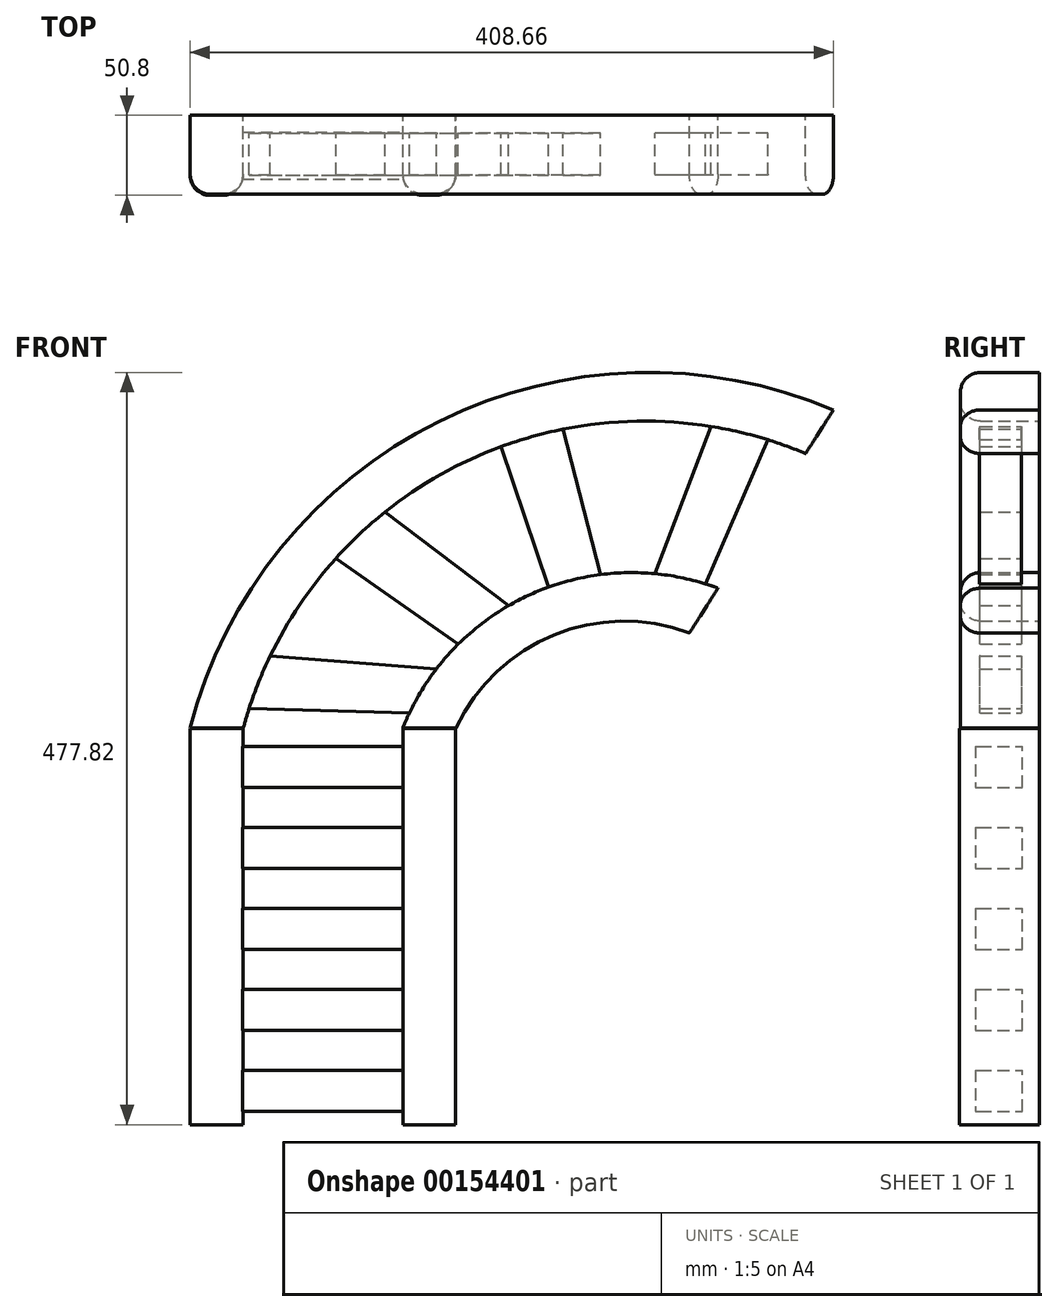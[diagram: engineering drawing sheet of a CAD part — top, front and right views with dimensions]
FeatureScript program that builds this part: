
annotation { "Feature Type Name" : "Feature", "Feature Type Description" : "" }
export const myFeature = defineFeature(function(context is Context, id is Id, definition is map)
    precondition{}
    {
        {
            var Q0;
            Q0=qCreatedBy(makeId("Front.planeOp"),FACE);
            var sketch = newSketch(context, id + "F0", { "sketchPlane" : qUnion([Q0])});
            skLineSegment(sketch, "E0.bottom", {"start": v(-91.03, -95.5) * mm, "end": v(-57.46, -95.5) * mm});
            skLineSegment(sketch, "E0.top", {"start": v(-91.03, 156.28) * mm, "end": v(-57.46, 156.28) * mm});
            skLineSegment(sketch, "E0.left", {"start": v(-91.03, -95.5) * mm, "end": v(-91.03, 156.28) * mm});
            skLineSegment(sketch, "E0.right", {"start": v(-57.46, -95.5) * mm, "end": v(-57.46, 156.28) * mm});
            skLineSegment(sketch, "E1.bottom", {"start": v(44.14, -95.5) * mm, "end": v(77.55, -95.5) * mm});
            skLineSegment(sketch, "E1.top", {"start": v(44.14, 156.28) * mm, "end": v(77.55, 156.28) * mm});
            skLineSegment(sketch, "E1.left", {"start": v(44.14, -95.5) * mm, "end": v(44.14, 156.28) * mm});
            skLineSegment(sketch, "E1.right", {"start": v(77.55, -95.5) * mm, "end": v(77.55, 156.28) * mm});
            skSolve(sketch);
        }
        {
            var Q0;
            Q0=qSketchRegion(id+"F0",true);
            extrude(context, id + "F1", {"entities" : qUnion([Q0]), "depth" : 50.8 * mm});
        }
        {
            var Q0;
            Q0=qCreatedBy(makeId("Front.planeOp"),FACE);
            var sketch = newSketch(context, id + "F2", { "sketchPlane" : qUnion([Q0])});
            skLineSegment(sketch, "E2.bottom", {"start": v(-57.93, -87.01) * mm, "end": v(44.5, -87.01) * mm});
            skLineSegment(sketch, "E2.top", {"start": v(-57.93, -60.98) * mm, "end": v(44.5, -60.98) * mm});
            skLineSegment(sketch, "E2.left", {"start": v(-57.93, -87.01) * mm, "end": v(-57.93, -60.98) * mm});
            skLineSegment(sketch, "E2.right", {"start": v(44.5, -87.01) * mm, "end": v(44.5, -60.98) * mm});
            skLineSegment(sketch, "E3.bottom", {"start": v(-57.93, -35.58) * mm, "end": v(44.5, -35.58) * mm});
            skLineSegment(sketch, "E3.top", {"start": v(-57.93, -9.54) * mm, "end": v(44.5, -9.54) * mm});
            skLineSegment(sketch, "E3.left", {"start": v(-57.93, -35.58) * mm, "end": v(-57.93, -9.54) * mm});
            skLineSegment(sketch, "E3.right", {"start": v(44.5, -35.58) * mm, "end": v(44.5, -9.54) * mm});
            skLineSegment(sketch, "E4.bottom", {"start": v(-57.93, 15.86) * mm, "end": v(44.5, 15.86) * mm});
            skLineSegment(sketch, "E4.top", {"start": v(-57.93, 41.9) * mm, "end": v(44.5, 41.9) * mm});
            skLineSegment(sketch, "E4.left", {"start": v(-57.93, 15.86) * mm, "end": v(-57.93, 41.9) * mm});
            skLineSegment(sketch, "E4.right", {"start": v(44.5, 15.86) * mm, "end": v(44.5, 41.9) * mm});
            skLineSegment(sketch, "E5.bottom", {"start": v(-57.93, 67.3) * mm, "end": v(44.5, 67.3) * mm});
            skLineSegment(sketch, "E5.top", {"start": v(-57.93, 93.33) * mm, "end": v(44.5, 93.33) * mm});
            skLineSegment(sketch, "E5.left", {"start": v(-57.93, 67.3) * mm, "end": v(-57.93, 93.33) * mm});
            skLineSegment(sketch, "E5.right", {"start": v(44.5, 67.3) * mm, "end": v(44.5, 93.33) * mm});
            skLineSegment(sketch, "E6.bottom", {"start": v(-57.93, 118.73) * mm, "end": v(44.5, 118.73) * mm});
            skLineSegment(sketch, "E6.top", {"start": v(-57.93, 144.76) * mm, "end": v(44.5, 144.76) * mm});
            skLineSegment(sketch, "E6.left", {"start": v(-57.93, 118.73) * mm, "end": v(-57.93, 144.76) * mm});
            skLineSegment(sketch, "E6.right", {"start": v(44.5, 118.73) * mm, "end": v(44.5, 144.76) * mm});
            skSolve(sketch);
        }
        {
            var Q0;
            Q0=qSketchRegion(id+"F2",true);
            extrude(context, id + "F3", {"entities" : qUnion([Q0]), "operationType" : NewBodyOperationType.ADD, "depth" : 40.64 * mm, "hasSecondDirection" : true, "secondDirectionOppositeDirection" : false, "secondDirectionDepth" : 10.8 * mm});
        }
        {
            var Q0;
            Q0=makeQuery(id+"F1.opExtrude","SWEPT_BODY",BODY,{"disambiguationData":[OSD([sQuery(id+"F0.wireOp",EDGE,"E0.bottom"),sQuery(id+"F0.wireOp",EDGE,"E0.top"),sQuery(id+"F0.wireOp",EDGE,"E0.left"),sQuery(id+"F0.wireOp",EDGE,"E0.right")])]});
            var Q1;
            Q1=qCreatedBy(makeId("Right.planeOp"),FACE);
            mirror(context, id + "F4", {"entities" : qUnion([Q0]), "mirrorPlane" : qUnion([Q1])});
        }
        {
            var Q0;
            Q0=makeQuery(id+"F1.opExtrude","SWEPT_BODY",BODY,{"disambiguationData":[OSD([sQuery(id+"F0.wireOp",EDGE,"E0.bottom"),sQuery(id+"F0.wireOp",EDGE,"E0.top"),sQuery(id+"F0.wireOp",EDGE,"E0.left"),sQuery(id+"F0.wireOp",EDGE,"E0.right")])]});
            var Q1;
            Q1=qCreatedBy(makeId("Top.planeOp"),FACE);
            mirror(context, id + "F5", {"entities" : qUnion([Q0]), "mirrorPlane" : qUnion([Q1])});
        }
        {
            var Q0;
            Q0=makeQuery(id+"F1.opExtrude","SWEPT_BODY",BODY,{"disambiguationData":[OSD([sQuery(id+"F0.wireOp",EDGE,"E0.bottom"),sQuery(id+"F0.wireOp",EDGE,"E0.top"),sQuery(id+"F0.wireOp",EDGE,"E0.left"),sQuery(id+"F0.wireOp",EDGE,"E0.right")])]});
            var Q1;
            Q1=qCreatedBy(makeId("Right.planeOp"),FACE);
            mirror(context, id + "F6", {"entities" : qUnion([Q0]), "mirrorPlane" : qUnion([Q1])});
        }
        {
            var Q0;
            Q0=makeQuery(id+"F6.opPattern","COPY",BODY,{"derivedFrom":makeQuery(id+"F1.opExtrude","SWEPT_BODY",BODY,{"disambiguationData":[OSD([sQuery(id+"F0.wireOp",EDGE,"E0.bottom"),sQuery(id+"F0.wireOp",EDGE,"E0.top"),sQuery(id+"F0.wireOp",EDGE,"E0.left"),sQuery(id+"F0.wireOp",EDGE,"E0.right")])]}),"instanceName":"1"});
            deleteBodies(context, id + "F7", {"entities" : qUnion([Q0])});
        }
        {
            var Q0;
            Q0=makeQuery(id+"F5.opPattern","COPY",BODY,{"derivedFrom":makeQuery(id+"F1.opExtrude","SWEPT_BODY",BODY,{"disambiguationData":[OSD([sQuery(id+"F0.wireOp",EDGE,"E0.bottom"),sQuery(id+"F0.wireOp",EDGE,"E0.top"),sQuery(id+"F0.wireOp",EDGE,"E0.left"),sQuery(id+"F0.wireOp",EDGE,"E0.right")])]}),"instanceName":"1"});
            deleteBodies(context, id + "F8", {"entities" : qUnion([Q0])});
        }
        {
            var Q0;
            Q0=makeQuery(id+"F4.opPattern","COPY",BODY,{"derivedFrom":makeQuery(id+"F1.opExtrude","SWEPT_BODY",BODY,{"disambiguationData":[OSD([sQuery(id+"F0.wireOp",EDGE,"E0.bottom"),sQuery(id+"F0.wireOp",EDGE,"E0.top"),sQuery(id+"F0.wireOp",EDGE,"E0.left"),sQuery(id+"F0.wireOp",EDGE,"E0.right")])]}),"instanceName":"1"});
            deleteBodies(context, id + "F9", {"entities" : qUnion([Q0])});
        }
        {
            var Q0;
            Q0=qCreatedBy(makeId("Front.planeOp"),FACE);
            var sketch = newSketch(context, id + "F10", { "sketchPlane" : qUnion([Q0])});
            skLineSegment(sketch, "E7", {"start": v(-90.93, 156.43) * mm, "end": v(-57.18, 156.43) * mm});
            skArc(sketch, "E8", {"start": v(317.63, 358.53) * mm, "mid": v(67.02, 351.13) * mm, "end": v(-90.93, 156.43) * mm});
            skArc(sketch, "E9", {"start": v(299.95, 330.76) * mm, "mid": v(81.84, 324.62) * mm, "end": v(-57.18, 156.43) * mm});
            skLineSegment(sketch, "E10", {"start": v(317.63, 358.53) * mm, "end": v(299.95, 330.76) * mm});
            skLineSegment(sketch, "E11", {"start": v(44.1, 156.43) * mm, "end": v(77.86, 156.43) * mm});
            skArc(sketch, "E12", {"start": v(244.3, 245.29) * mm, "mid": v(126.08, 241.68) * mm, "end": v(44.1, 156.43) * mm});
            skLineSegment(sketch, "E13", {"start": v(244.3, 245.29) * mm, "end": v(226.17, 216.79) * mm});
            skArc(sketch, "E14", {"start": v(226.17, 216.79) * mm, "mid": v(140.2, 215.61) * mm, "end": v(77.86, 156.43) * mm});
            skSolve(sketch);
        }
        {
            var Q0;
            Q0=qSketchRegion(id+"F10",true);
            extrude(context, id + "F11", {"entities" : qUnion([Q0]), "depth" : 50.16 * mm});
        }
        {
            var Q0;
            Q0=qCreatedBy(makeId("Front.planeOp"),FACE);
            var sketch = newSketch(context, id + "F12", { "sketchPlane" : qUnion([Q0])});
            skLineSegment(sketch, "E15", {"start": v(-58.79, 169.05) * mm, "end": v(51.94, 165.92) * mm});
            skArc(sketch, "E16", {"start": v(-43.86, 202.37) * mm, "mid": v(-52.52, 186.25) * mm, "end": v(-58.79, 169.05) * mm});
            skLineSegment(sketch, "E17", {"start": v(-43.86, 202.37) * mm, "end": v(69.98, 193.7) * mm});
            skArc(sketch, "E18", {"start": v(51.94, 165.92) * mm, "mid": v(61.37, 179.54) * mm, "end": v(69.98, 193.7) * mm});
            skLineSegment(sketch, "E19", {"start": v(-3.25, 267.62) * mm, "end": v(82.83, 207.23) * mm});
            skArc(sketch, "E20", {"start": v(31.11, 295.04) * mm, "mid": v(11.47, 284.41) * mm, "end": v(-3.25, 267.62) * mm});
            skLineSegment(sketch, "E21", {"start": v(31.11, 295.04) * mm, "end": v(115.1, 231.18) * mm});
            skArc(sketch, "E22", {"start": v(82.83, 207.23) * mm, "mid": v(100.38, 217.3) * mm, "end": v(115.1, 231.18) * mm});
            skLineSegment(sketch, "E23", {"start": v(104.23, 342.23) * mm, "end": v(137.7, 242.57) * mm});
            skArc(sketch, "E24", {"start": v(143.94, 353.26) * mm, "mid": v(123.43, 350.1) * mm, "end": v(104.23, 342.23) * mm});
            skLineSegment(sketch, "E25", {"start": v(143.94, 353.26) * mm, "end": v(170.79, 249.56) * mm});
            skArc(sketch, "E26", {"start": v(137.7, 242.57) * mm, "mid": v(154.64, 244.17) * mm, "end": v(170.79, 249.56) * mm});
            skArc(sketch, "E27", {"start": v(279.48, 347.83) * mm, "mid": v(262.24, 354.81) * mm, "end": v(244.09, 358.84) * mm});
            skLineSegment(sketch, "E28", {"start": v(244.09, 358.84) * mm, "end": v(202.41, 249.93) * mm});
            skLineSegment(sketch, "E29", {"start": v(279.48, 347.83) * mm, "end": v(233.08, 240.46) * mm});
            skArc(sketch, "E30", {"start": v(202.41, 249.93) * mm, "mid": v(217.3, 243.75) * mm, "end": v(233.08, 240.46) * mm});
            skSolve(sketch);
        }
        {
            var Q0;
            Q0=qSketchRegion(id+"F12",true);
            extrude(context, id + "F13", {"entities" : qUnion([Q0]), "operationType" : NewBodyOperationType.ADD, "depth" : 38.1 * mm, "hasSecondDirection" : true, "secondDirectionOppositeDirection" : false, "secondDirectionDepth" : 11.43 * mm});
        }
        {
            var Q0;
            Q0=makeQuery(id+"F1.opExtrude","CAP_EDGE",EDGE,{"disambiguationData":[OSD([sQuery(id+"F0.wireOp",EDGE,"E0.right")])],"isStart":false});
            var Q1;
            Q1=makeQuery(id+"F1.opExtrude","CAP_EDGE",EDGE,{"disambiguationData":[OSD([sQuery(id+"F0.wireOp",EDGE,"E1.left")])],"isStart":false});
            var Q2;
            Q2=makeQuery(id+"F11.opExtrude","CAP_EDGE",EDGE,{"disambiguationData":[OSD([sQuery(id+"F10.wireOp",EDGE,"E9")])],"isStart":false});
            var Q3;
            Q3=makeQuery(id+"F11.opExtrude","CAP_EDGE",EDGE,{"disambiguationData":[OSD([sQuery(id+"F10.wireOp",EDGE,"E12")])],"isStart":false});
            fillet(context, id + "F14", {"entities" : qUnion([Q0, Q1, Q2, Q3]), "radius" : 12.7 * mm, "tangentPropagation" : true, "allowEdgeOverflow" : false});
        }
        {
            var Q0;
            Q0=makeQuery(id+"F11.opExtrude","CAP_EDGE",EDGE,{"disambiguationData":[OSD([sQuery(id+"F10.wireOp",EDGE,"E8")])],"isStart":false});
            var Q1;
            Q1=makeQuery(id+"F1.opExtrude","CAP_EDGE",EDGE,{"disambiguationData":[OSD([sQuery(id+"F0.wireOp",EDGE,"E0.left")])],"isStart":false});
            var Q2;
            Q2=makeQuery(id+"F1.opExtrude","CAP_EDGE",EDGE,{"disambiguationData":[OSD([sQuery(id+"F0.wireOp",EDGE,"E1.right")])],"isStart":false});
            var Q3;
            Q3=makeQuery(id+"F11.opExtrude","CAP_EDGE",EDGE,{"disambiguationData":[OSD([sQuery(id+"F10.wireOp",EDGE,"E14")])],"isStart":false});
            fillet(context, id + "F15", {"entities" : qUnion([Q0, Q1, Q2, Q3]), "radius" : 12.7 * mm, "tangentPropagation" : true, "allowEdgeOverflow" : false});
        }
    });
